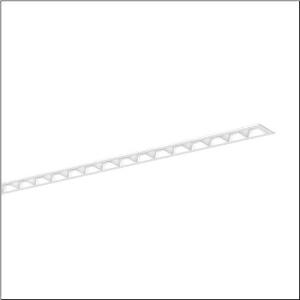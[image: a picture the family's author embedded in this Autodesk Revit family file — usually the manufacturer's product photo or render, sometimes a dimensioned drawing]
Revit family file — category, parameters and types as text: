
# Revit family: silica_r__21_51mx16dc4awb_037f
name_source: partatom
category: Lighting Fixtures
units: mm (PartAtom-declared; Revit-internal decimal feet)

## family parameters
Cut with Voids When Loaded = No
Host = Face
Light Source = No
Part Type = Normal
Room Calculation Point = No
Round Connector Dimension = Use Diameter
Shared = No

## types (1)
- --- (1 x LED, 10800 lm, 60.6 W, 4000K)
    Apparent Load = 61 VA
    CIE Flux Codes = 83 98 100 100 100
    Color Rendering = 80
    Color Temperature = 4000K
    Default Elevation = 1800 mm
    Description = Silica® 21, office luminaire, primary light control with darklight reflector, of PMMA, white, CAT 2 (L<= 3000cd/m²), light emission: direct distribution, primary light characteristic: symmetric, installation type: recessed, LED, rated luminous flux: 10.800lm, luminous efficacy: 178lm/W, light colour: 840, colour temperature: 4000K, with terminal, 3+2-pole, max. 2.5mm², mains connection: 220..240V, AC, 50/60Hz, rated input power: 60.6W, luminaire housing, of aluminium, traffic white (RAL 9016), length: 3.028mm, width: 79mm, height: 53mm, protection rating (complete): IP20, insulation class (complete): insulation class I (protective earthing), certification: CE, permissible operating ambient temperature: 0..+35°C, standard: EN 50419, packaging unit: 1 piece
    Height = 0 mm  [stored 0 ft]
    Lamp = 1 x LED
    Lamp Light Flux = 10800 lm
    Lamp Power = 60.6 W
    Lamp count = 1
    Length = 3027 mm
    Luminous efficacy = 178 lm/W
    Manufacturer = Siteco
    ModVariant = No
    Model = 51MX16DC4AWB
    Mounting Place = Ceiling
    Mounting Type = Recessed
    Number of Poles = 1
    OnlyDefault = Yes
    Power Factor = 1
    Product Name = Silica® 21
    Product group = office luminaire | ceiling recessed
    ProductGroupID = 401
    Protection Class = Protection class I
    Protection Degree = IP 20
    RLX_Detail_Level = 1
    RLX_Emergency_Light_Flux = 0 lm
    RLX_Emergency_Type = 0
    RLX_Emergency_Type_DB = No
    RlxData = <blob elided: 60021 chars, md5=26618ae7>
    Socket = socket
    Standby Power = 0 W
    System Light Flux = 10800 lm
    System Power = 61 W
    Type Comments = factory setting: luminous flux: 100 % | dim-lin: 254 | 336 mA
    Type Image = l_1297786.jpg
    URL = http://relux.com
    VarID = @adj_055073
    Voltage = 0 V
    Weight = 0.00 kg
    Width = 79 mm

note: [stored X ft] marks values corroborated as IEEE doubles in the binary element streams (Revit-internal decimal feet)

## geometry (parser evidence)
native form markers: Blend x4, Sweep x11
no freeform markers — native parametric forms only
